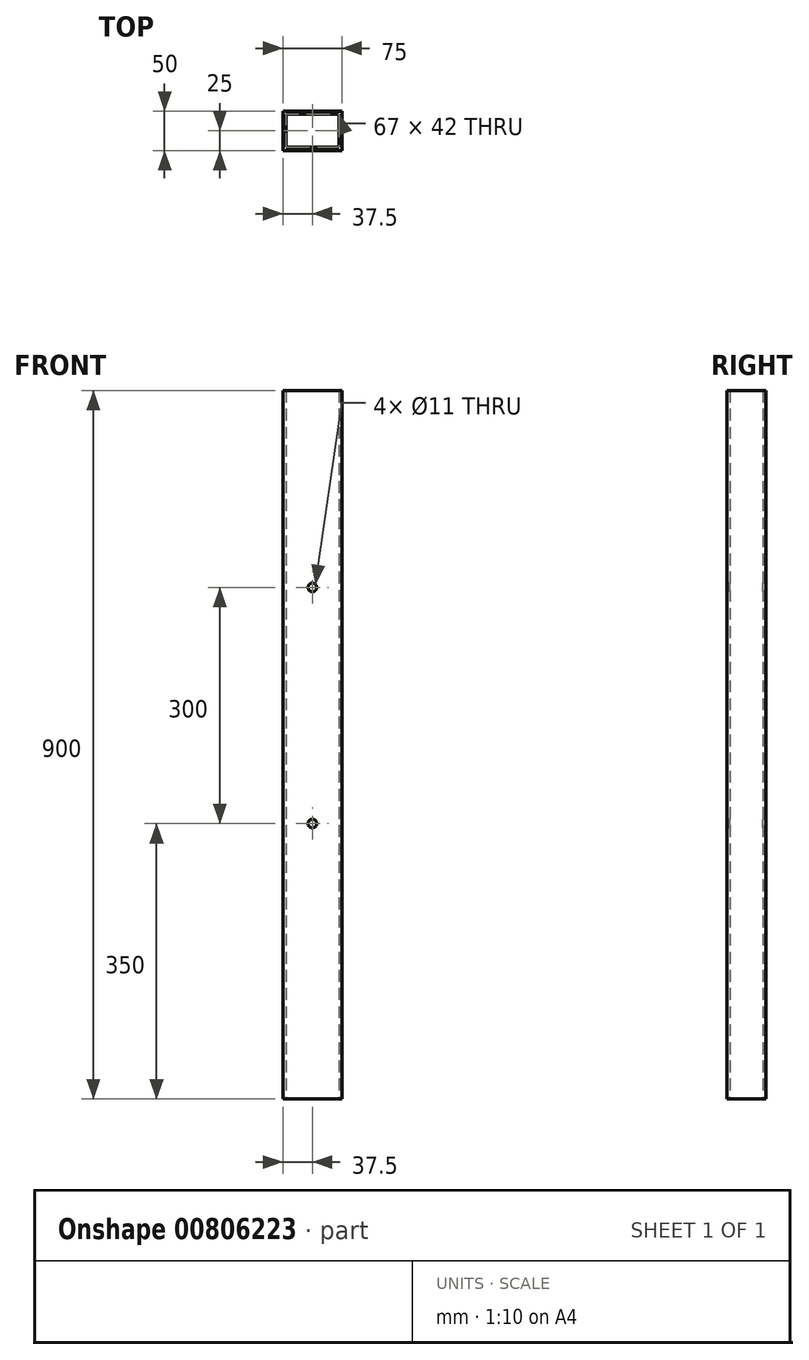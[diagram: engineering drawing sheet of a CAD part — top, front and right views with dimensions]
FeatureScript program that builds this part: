
annotation { "Feature Type Name" : "Feature", "Feature Type Description" : "" }
export const myFeature = defineFeature(function(context is Context, id is Id, definition is map)
    precondition{}
    {
        {
            var Q0;
            Q0=qCreatedBy(makeId("Top.planeOp"),FACE);
            var sketch = newSketch(context, id + "F0", { "sketchPlane" : qUnion([Q0])});
            skLineSegment(sketch, "E0.bottom", {"start": v(37.5, -25) * mm, "end": v(-37.5, -25) * mm});
            skLineSegment(sketch, "E0.top", {"start": v(37.5, 25) * mm, "end": v(-37.5, 25) * mm});
            skLineSegment(sketch, "E0.left", {"start": v(37.5, -25) * mm, "end": v(37.5, 25) * mm});
            skLineSegment(sketch, "E0.right", {"start": v(-37.5, -25) * mm, "end": v(-37.5, 25) * mm});
            skPoint(sketch, "E0.middle", {"position": v(0, 0) * mm});
            skLineSegment(sketch, "E1.0", {"start": v(33.5, 21) * mm, "end": v(-33.5, 21) * mm});
            skLineSegment(sketch, "E1.1", {"start": v(33.5, -21) * mm, "end": v(33.5, 21) * mm});
            skLineSegment(sketch, "E1.2", {"start": v(33.5, -21) * mm, "end": v(-33.5, -21) * mm});
            skLineSegment(sketch, "E1.3", {"start": v(-33.5, -21) * mm, "end": v(-33.5, 21) * mm});
            skSolve(sketch);
        }
        {
            var Q0;
            Q0=qSketchRegion(id+"F0",true);
            extrude(context, id + "F1", {"entities" : qUnion([Q0]), "depth" : 900 * mm, "offsetDistance" : 25 * mm});
        }
        {
            var Q0;
            Q0=makeQuery(id+"F1.opExtrude","SWEPT_FACE",FACE,{"disambiguationData":[OSD([sQuery(id+"F0.wireOp",EDGE,"E0.bottom")])]});
            var sketch = newSketch(context, id + "F2", { "sketchPlane" : qUnion([Q0])});
            skLineSegment(sketch, "E2", {"start": v(0, 0) * mm, "end": v(0, 350) * mm, "construction": true});
            skCircle(sketch, "E3", {"center": v(0, 350) * mm, "radius": 5.5 * mm});
            skLineSegment(sketch, "E4", {"start": v(0, 0) * mm, "end": v(0, 650) * mm, "construction": true});
            skCircle(sketch, "E5", {"center": v(0, 650) * mm, "radius": 5.5 * mm});
            skSolve(sketch);
        }
        {
            var Q0;
            Q0=makeQuery(id+"F2.imprint","IMPRINT",FACE,{"disambiguationData":[TD([[makeQuery(id+"F2.imprint","IMPRINT",EDGE,{"derivedFrom":sQuery(id+"F2.wireOp",EDGE,"E3")}),1.0]])]});
            var Q1;
            Q1=makeQuery(id+"F2.imprint","IMPRINT",FACE,{"disambiguationData":[TD([[makeQuery(id+"F2.imprint","IMPRINT",EDGE,{"derivedFrom":sQuery(id+"F2.wireOp",EDGE,"E5")}),1.0]])]});
            extrude(context, id + "F3", {"entities" : qUnion([Q0, Q1]), "operationType" : NewBodyOperationType.REMOVE, "oppositeDirection" : true, "depth" : 50 * mm, "offsetDistance" : 25 * mm});
        }
    });
